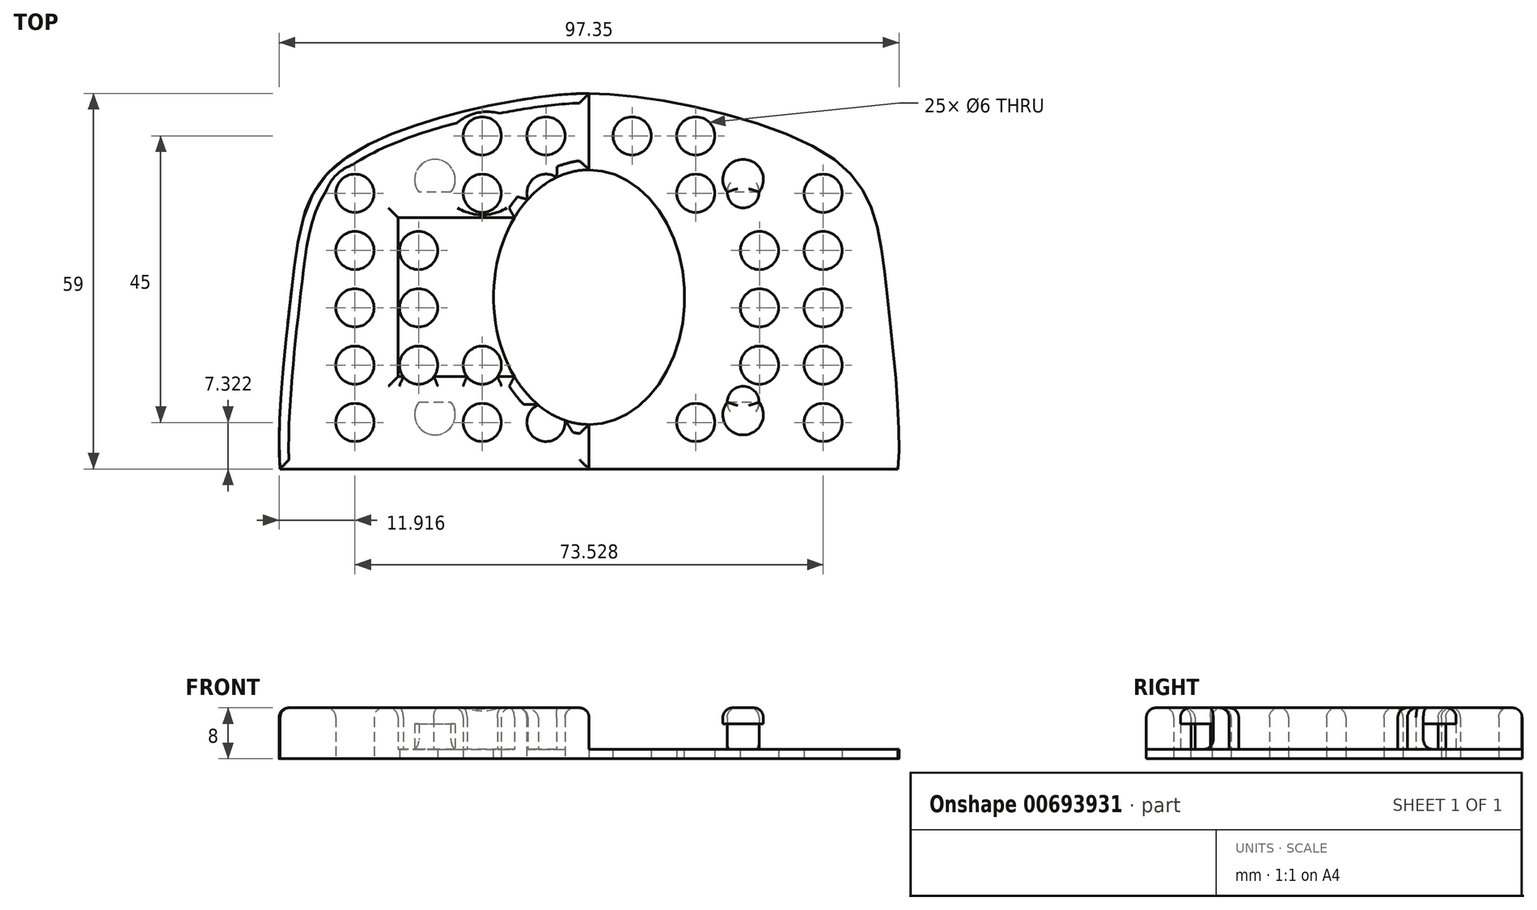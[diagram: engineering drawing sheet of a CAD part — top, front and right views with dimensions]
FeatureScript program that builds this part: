
annotation { "Feature Type Name" : "Feature", "Feature Type Description" : "" }
export const myFeature = defineFeature(function(context is Context, id is Id, definition is map)
    precondition{}
    {
        {
            var Q0;
            Q0=qCreatedBy(makeId("Top.planeOp"),FACE);
            var sketch = newSketch(context, id + "F0", { "sketchPlane" : qUnion([Q0])});
            skLineSegment(sketch, "E0", {"start": v(-48.5, 0) * mm, "end": v(48.5, 0) * mm});
            skLineSegment(sketch, "E1", {"start": v(0, 0) * mm, "end": v(0, 59) * mm});
            skFitSpline(sketch, "E2", {"points": [v(-48.5, 0) * mm, v(-46.5, 30) * mm, v(-38, 49) * mm, v(0, 59) * mm], "startDerivative": vector(-6.1, 58.21) * mm, "endDerivative": vector(65.23, -0.68) * mm});
            skFitSpline(sketch, "E3.MirrorCS", {"points": [v(48.5, 0) * mm, v(46.5, 30) * mm, v(38, 49) * mm, v(0, 59) * mm], "startDerivative": vector(6.1, 58.21) * mm, "endDerivative": vector(-65.23, -0.68) * mm});
            skEllipse(sketch, "E4", {"center": v(0, 27) * mm, "majorRadius": 20 * mm, "minorRadius": 15 * mm, "majorAxis": v(0, 1)});
            skLineSegment(sketch, "E5.bottom", {"start": v(30, 39.5) * mm, "end": v(-30, 39.5) * mm});
            skLineSegment(sketch, "E5.top", {"start": v(30, 14.5) * mm, "end": v(-30, 14.5) * mm});
            skLineSegment(sketch, "E5.left", {"start": v(30, 39.5) * mm, "end": v(30, 14.5) * mm});
            skLineSegment(sketch, "E5.right", {"start": v(-30, 39.5) * mm, "end": v(-30, 14.5) * mm});
            skArc(sketch, "E6", {"start": v(-26.7, 43.5) * mm, "mid": v(-24.2, 41) * mm, "end": v(-21.7, 43.5) * mm});
            skLineSegment(sketch, "E7", {"start": v(-26.7, 43.5) * mm, "end": v(-21.7, 43.5) * mm});
            skLineSegment(sketch, "E8", {"start": v(0, 27) * mm, "end": v(-30, 27) * mm});
            skArc(sketch, "E9.MirrorC", {"start": v(-26.7, 10.5) * mm, "mid": v(-24.2, 13) * mm, "end": v(-21.7, 10.5) * mm});
            skLineSegment(sketch, "E10.MirrorCS", {"start": v(-26.7, 10.5) * mm, "end": v(-21.7, 10.5) * mm});
            skLineSegment(sketch, "E11.MirrorCS", {"start": v(0, 54) * mm, "end": v(0, -5) * mm});
            skArc(sketch, "E12.MirrorC", {"start": v(26.7, 43.5) * mm, "mid": v(24.2, 41) * mm, "end": v(21.7, 43.5) * mm});
            skLineSegment(sketch, "E13.MirrorCS", {"start": v(26.7, 43.5) * mm, "end": v(21.7, 43.5) * mm});
            skArc(sketch, "E14.MirrorC", {"start": v(26.7, 10.5) * mm, "mid": v(24.2, 13) * mm, "end": v(21.7, 10.5) * mm});
            skLineSegment(sketch, "E15.MirrorCS", {"start": v(26.7, 10.5) * mm, "end": v(21.7, 10.5) * mm});
            skCircle(sketch, "E16", {"center": v(-6.76, 52.32) * mm, "radius": 3 * mm});
            skCircle(sketch, "E17.0.1.0", {"center": v(-6.76, 43.32) * mm, "radius": 3 * mm});
            skCircle(sketch, "E17.0.2.0", {"center": v(-6.76, 34.32) * mm, "radius": 3 * mm});
            skCircle(sketch, "E17.0.3.0", {"center": v(-6.76, 25.32) * mm, "radius": 3 * mm});
            skCircle(sketch, "E17.0.4.0", {"center": v(-6.76, 16.32) * mm, "radius": 3 * mm});
            skCircle(sketch, "E17.0.5.0", {"center": v(-6.76, 7.32) * mm, "radius": 3 * mm});
            skCircle(sketch, "E17.1.0.0", {"center": v(-16.76, 52.32) * mm, "radius": 3 * mm});
            skCircle(sketch, "E17.1.1.0", {"center": v(-16.76, 43.32) * mm, "radius": 3 * mm});
            skCircle(sketch, "E17.1.2.0", {"center": v(-16.76, 34.32) * mm, "radius": 3 * mm});
            skCircle(sketch, "E17.1.3.0", {"center": v(-16.76, 25.32) * mm, "radius": 3 * mm});
            skCircle(sketch, "E17.1.4.0", {"center": v(-16.76, 16.32) * mm, "radius": 3 * mm});
            skCircle(sketch, "E17.1.5.0", {"center": v(-16.76, 7.32) * mm, "radius": 3 * mm});
            skCircle(sketch, "E17.2.2.0", {"center": v(-26.76, 34.32) * mm, "radius": 3 * mm});
            skCircle(sketch, "E17.2.3.0", {"center": v(-26.76, 25.32) * mm, "radius": 3 * mm});
            skCircle(sketch, "E17.2.4.0", {"center": v(-26.76, 16.32) * mm, "radius": 3 * mm});
            skCircle(sketch, "E17.3.1.0", {"center": v(-36.76, 43.32) * mm, "radius": 3 * mm});
            skCircle(sketch, "E17.3.2.0", {"center": v(-36.76, 34.32) * mm, "radius": 3 * mm});
            skCircle(sketch, "E17.3.3.0", {"center": v(-36.76, 25.32) * mm, "radius": 3 * mm});
            skCircle(sketch, "E17.3.4.0", {"center": v(-36.76, 16.32) * mm, "radius": 3 * mm});
            skCircle(sketch, "E17.3.5.0", {"center": v(-36.76, 7.32) * mm, "radius": 3 * mm});
            skLineSegment(sketch, "E17.direction1", {"start": v(-6.76, 52.32) * mm, "end": v(-16.76, 52.32) * mm, "construction": true});
            skLineSegment(sketch, "E17.direction2", {"start": v(-6.76, 52.32) * mm, "end": v(-6.76, 43.32) * mm, "construction": true});
            skCircle(sketch, "E18.MirrorC", {"center": v(6.76, 52.32) * mm, "radius": 3 * mm});
            skCircle(sketch, "E19.MirrorC", {"center": v(16.76, 52.32) * mm, "radius": 3 * mm});
            skCircle(sketch, "E20.MirrorC", {"center": v(16.76, 43.32) * mm, "radius": 3 * mm});
            skCircle(sketch, "E21.MirrorC", {"center": v(36.76, 43.32) * mm, "radius": 3 * mm});
            skCircle(sketch, "E22.MirrorC", {"center": v(6.76, 43.32) * mm, "radius": 3 * mm});
            skCircle(sketch, "E23.MirrorC", {"center": v(6.76, 34.32) * mm, "radius": 3 * mm});
            skCircle(sketch, "E24.MirrorC", {"center": v(16.76, 34.32) * mm, "radius": 3 * mm});
            skCircle(sketch, "E25.MirrorC", {"center": v(26.76, 34.32) * mm, "radius": 3 * mm});
            skCircle(sketch, "E26.MirrorC", {"center": v(36.76, 34.32) * mm, "radius": 3 * mm});
            skCircle(sketch, "E27.MirrorC", {"center": v(36.76, 25.32) * mm, "radius": 3 * mm});
            skCircle(sketch, "E28.MirrorC", {"center": v(26.76, 25.32) * mm, "radius": 3 * mm});
            skCircle(sketch, "E29.MirrorC", {"center": v(16.76, 25.32) * mm, "radius": 3 * mm});
            skCircle(sketch, "E30.MirrorC", {"center": v(6.76, 25.32) * mm, "radius": 3 * mm});
            skCircle(sketch, "E31.MirrorC", {"center": v(6.76, 16.32) * mm, "radius": 3 * mm});
            skCircle(sketch, "E32.MirrorC", {"center": v(16.76, 16.32) * mm, "radius": 3 * mm});
            skCircle(sketch, "E33.MirrorC", {"center": v(26.76, 16.32) * mm, "radius": 3 * mm});
            skCircle(sketch, "E34.MirrorC", {"center": v(36.76, 16.32) * mm, "radius": 3 * mm});
            skCircle(sketch, "E35.MirrorC", {"center": v(36.76, 7.32) * mm, "radius": 3 * mm});
            skCircle(sketch, "E36.MirrorC", {"center": v(16.76, 7.32) * mm, "radius": 3 * mm});
            skCircle(sketch, "E37.MirrorC", {"center": v(6.76, 7.32) * mm, "radius": 3 * mm});
            skArc(sketch, "E38", {"start": v(-21.7, 43.5) * mm, "mid": v(-24.2, 48.64) * mm, "end": v(-26.7, 43.5) * mm});
            skArc(sketch, "E39.MirrorCS", {"start": v(21.7, 43.5) * mm, "mid": v(24.2, 48.64) * mm, "end": v(26.7, 43.5) * mm});
            skArc(sketch, "E40.MirrorCS", {"start": v(-21.7, 10.5) * mm, "mid": v(-24.2, 5.36) * mm, "end": v(-26.7, 10.5) * mm});
            skArc(sketch, "E41.MirrorCS", {"start": v(21.7, 10.5) * mm, "mid": v(24.2, 5.36) * mm, "end": v(26.7, 10.5) * mm});
            skSolve(sketch);
        }
        {
            var Q0;
            Q0 = qSketchRegion(id + "F0", true);
            var Q1;
            {var subQ0=sQuery(id+"F0.wireOp",EDGE,"E5.bottom");var subQ1=sQuery(id+"F0.wireOp",EDGE,"E4");var subQ2=makeQuery(id+"F0.imprint","INTERSECT",VERTEX,{"disambiguationData":[OD(0.0)],"derivedFrom":[subQ1,subQ0]});Q1=makeQuery(id+"F0.imprint","IMPRINT",FACE,{"disambiguationData":[TD([[makeQuery(id+"F0.imprint","IMPRINT",EDGE,{"disambiguationData":[TD([[subQ2,-1.0]])],"derivedFrom":subQ1}),-1.0]])]});}
            var Q2;
            {var subQ5=sQuery(id+"F0.wireOp",EDGE,"E5.left");Q2=makeQuery(id+"F0.imprint","IMPRINT",FACE,{"disambiguationData":[TD([[makeQuery(id+"F0.imprint","IMPRINT",EDGE,{"derivedFrom":subQ5}),-1.0]])]});}
            var Q3;
            {var subQ8=sQuery(id+"F0.wireOp",EDGE,"E17.1.3.0");var subQ9=sQuery(id+"F0.wireOp",EDGE,"E4");var subQ10=makeQuery(id+"F0.imprint","INTERSECT",VERTEX,{"disambiguationData":[OD(1.0)],"derivedFrom":[subQ9,subQ8]});Q3=makeQuery(id+"F0.imprint","IMPRINT",FACE,{"disambiguationData":[TD([[makeQuery(id+"F0.imprint","IMPRINT",EDGE,{"disambiguationData":[TD([[subQ10,-1.0]])],"derivedFrom":subQ9}),-1.0]])]});}
            var Q4;
            {var subQ0=sQuery(id+"F0.wireOp",EDGE,"E8");var subQ1=sQuery(id+"F0.wireOp",EDGE,"E4");var subQ2=makeQuery(id+"F0.imprint","INTERSECT",VERTEX,{"derivedFrom":[subQ1,subQ0]});Q4=makeQuery(id+"F0.imprint","IMPRINT",FACE,{"disambiguationData":[TD([[makeQuery(id+"F0.imprint","IMPRINT",EDGE,{"disambiguationData":[TD([[subQ2,-1.0]])],"derivedFrom":subQ1}),-1.0]])]});}
            var Q5;
            {var subQ0=sQuery(id+"F0.wireOp",EDGE,"E17.1.3.0");var subQ1=sQuery(id+"F0.wireOp",EDGE,"E4");var subQ2=makeQuery(id+"F0.imprint","INTERSECT",VERTEX,{"disambiguationData":[OD(0.0)],"derivedFrom":[subQ1,subQ0]});Q5=makeQuery(id+"F0.imprint","IMPRINT",FACE,{"disambiguationData":[TD([[makeQuery(id+"F0.imprint","IMPRINT",EDGE,{"disambiguationData":[TD([[subQ2,-1.0]])],"derivedFrom":subQ1}),-1.0]])]});}
            var Q6;
            {var subQ0=sQuery(id+"F0.wireOp",EDGE,"E17.0.1.0");var subQ1=sQuery(id+"F0.wireOp",EDGE,"E4");var subQ2=makeQuery(id+"F0.imprint","INTERSECT",VERTEX,{"disambiguationData":[OD(0.0)],"derivedFrom":[subQ1,subQ0]});Q6=makeQuery(id+"F0.imprint","IMPRINT",FACE,{"disambiguationData":[TD([[makeQuery(id+"F0.imprint","IMPRINT",EDGE,{"disambiguationData":[TD([[subQ2,-1.0]])],"derivedFrom":subQ1}),-1.0]])]});}
            var Q7;
            {var subQ0=sQuery(id+"F0.wireOp",EDGE,"E22.MirrorC");var subQ1=sQuery(id+"F0.wireOp",EDGE,"E4");var subQ2=makeQuery(id+"F0.imprint","INTERSECT",VERTEX,{"disambiguationData":[OD(0.0)],"derivedFrom":[subQ1,subQ0]});Q7=makeQuery(id+"F0.imprint","IMPRINT",FACE,{"disambiguationData":[TD([[makeQuery(id+"F0.imprint","IMPRINT",EDGE,{"disambiguationData":[TD([[subQ2,-1.0]])],"derivedFrom":subQ1}),-1.0]])]});}
            var Q8;
            {var subQ0=sQuery(id+"F0.wireOp",EDGE,"E17.0.5.0");var subQ1=sQuery(id+"F0.wireOp",EDGE,"E4");var subQ2=makeQuery(id+"F0.imprint","INTERSECT",VERTEX,{"disambiguationData":[OD(0.0)],"derivedFrom":[subQ1,subQ0]});Q8=makeQuery(id+"F0.imprint","IMPRINT",FACE,{"disambiguationData":[TD([[makeQuery(id+"F0.imprint","IMPRINT",EDGE,{"disambiguationData":[TD([[subQ2,-1.0]])],"derivedFrom":subQ1}),-1.0]])]});}
            var Q9;
            {var subQ0=sQuery(id+"F0.wireOp",EDGE,"E37.MirrorC");var subQ1=sQuery(id+"F0.wireOp",EDGE,"E4");var subQ2=makeQuery(id+"F0.imprint","INTERSECT",VERTEX,{"disambiguationData":[OD(0.0)],"derivedFrom":[subQ1,subQ0]});Q9=makeQuery(id+"F0.imprint","IMPRINT",FACE,{"disambiguationData":[TD([[makeQuery(id+"F0.imprint","IMPRINT",EDGE,{"disambiguationData":[TD([[subQ2,-1.0]])],"derivedFrom":subQ1}),-1.0]])]});}
            var Q10;
            {var subQ0=sQuery(id+"F0.wireOp",EDGE,"E29.MirrorC");var subQ1=sQuery(id+"F0.wireOp",EDGE,"E4");var subQ2=makeQuery(id+"F0.imprint","INTERSECT",VERTEX,{"disambiguationData":[OD(0.0)],"derivedFrom":[subQ1,subQ0]});Q10=makeQuery(id+"F0.imprint","IMPRINT",FACE,{"disambiguationData":[TD([[makeQuery(id+"F0.imprint","IMPRINT",EDGE,{"disambiguationData":[TD([[subQ2,-1.0]])],"derivedFrom":subQ1}),-1.0]])]});}
            var Q11;
            {var subQ0=sQuery(id+"F0.wireOp",EDGE,"E17.1.2.0");var subQ1=sQuery(id+"F0.wireOp",EDGE,"E4");var subQ2=makeQuery(id+"F0.imprint","INTERSECT",VERTEX,{"disambiguationData":[OD(0.0)],"derivedFrom":[subQ1,subQ0]});Q11=makeQuery(id+"F0.imprint","IMPRINT",FACE,{"disambiguationData":[TD([[makeQuery(id+"F0.imprint","IMPRINT",EDGE,{"disambiguationData":[TD([[subQ2,-1.0]])],"derivedFrom":subQ1}),-1.0]])]});}
            var Q12;
            {var subQ0=sQuery(id+"F0.wireOp",EDGE,"E24.MirrorC");var subQ1=sQuery(id+"F0.wireOp",EDGE,"E4");var subQ2=makeQuery(id+"F0.imprint","INTERSECT",VERTEX,{"disambiguationData":[OD(0.0)],"derivedFrom":[subQ1,subQ0]});Q12=makeQuery(id+"F0.imprint","IMPRINT",FACE,{"disambiguationData":[TD([[makeQuery(id+"F0.imprint","IMPRINT",EDGE,{"disambiguationData":[TD([[subQ2,-1.0]])],"derivedFrom":subQ1}),-1.0]])]});}
            var Q13;
            {var subQ0=sQuery(id+"F0.wireOp",EDGE,"E17.1.4.0");var subQ1=sQuery(id+"F0.wireOp",EDGE,"E5.top");var subQ2=makeQuery(id+"F0.imprint","INTERSECT",VERTEX,{"disambiguationData":[OD(0.0)],"derivedFrom":[subQ1,subQ0]});Q13=makeQuery(id+"F0.imprint","IMPRINT",FACE,{"disambiguationData":[TD([[makeQuery(id+"F0.imprint","IMPRINT",EDGE,{"disambiguationData":[TD([[subQ2,-1.0]])],"derivedFrom":subQ1}),-1.0]])]});}
            var Q14;
            {var subQ0=sQuery(id+"F0.wireOp",EDGE,"E32.MirrorC");var subQ1=sQuery(id+"F0.wireOp",EDGE,"E5.top");var subQ2=makeQuery(id+"F0.imprint","INTERSECT",VERTEX,{"disambiguationData":[OD(0.0)],"derivedFrom":[subQ1,subQ0]});Q14=makeQuery(id+"F0.imprint","IMPRINT",FACE,{"disambiguationData":[TD([[makeQuery(id+"F0.imprint","IMPRINT",EDGE,{"disambiguationData":[TD([[subQ2,-1.0]])],"derivedFrom":subQ1}),-1.0]])]});}
            var Q15;
            {var subQ0=sQuery(id+"F0.wireOp",EDGE,"E17.1.4.0");var subQ1=sQuery(id+"F0.wireOp",EDGE,"E5.top");var subQ2=makeQuery(id+"F0.imprint","INTERSECT",VERTEX,{"disambiguationData":[OD(0.0)],"derivedFrom":[subQ1,subQ0]});Q15=makeQuery(id+"F0.imprint","IMPRINT",FACE,{"disambiguationData":[TD([[makeQuery(id+"F0.imprint","IMPRINT",EDGE,{"disambiguationData":[TD([[subQ2,-1.0]])],"derivedFrom":subQ1}),1.0]])]});}
            var Q16;
            {var subQ0=sQuery(id+"F0.wireOp",EDGE,"E32.MirrorC");var subQ1=sQuery(id+"F0.wireOp",EDGE,"E5.top");var subQ2=makeQuery(id+"F0.imprint","INTERSECT",VERTEX,{"disambiguationData":[OD(0.0)],"derivedFrom":[subQ1,subQ0]});Q16=makeQuery(id+"F0.imprint","IMPRINT",FACE,{"disambiguationData":[TD([[makeQuery(id+"F0.imprint","IMPRINT",EDGE,{"disambiguationData":[TD([[subQ2,-1.0]])],"derivedFrom":subQ1}),1.0]])]});}
            var Q17;
            Q17=makeQuery(id+"F0.imprint","IMPRINT",FACE,{"disambiguationData":[TD([[makeQuery(id+"F0.imprint","IMPRINT",EDGE,{"derivedFrom":sQuery(id+"F0.wireOp",EDGE,"E6")}),1.0]])]});
            var Q18;
            Q18=makeQuery(id+"F0.imprint","IMPRINT",FACE,{"disambiguationData":[TD([[makeQuery(id+"F0.imprint","IMPRINT",EDGE,{"derivedFrom":sQuery(id+"F0.wireOp",EDGE,"E7")}),1.0]])]});
            var Q19;
            Q19=makeQuery(id+"F0.imprint","IMPRINT",FACE,{"disambiguationData":[TD([[makeQuery(id+"F0.imprint","IMPRINT",EDGE,{"derivedFrom":sQuery(id+"F0.wireOp",EDGE,"E13.MirrorCS")}),-1.0]])]});
            var Q20;
            Q20=makeQuery(id+"F0.imprint","IMPRINT",FACE,{"disambiguationData":[TD([[makeQuery(id+"F0.imprint","IMPRINT",EDGE,{"derivedFrom":sQuery(id+"F0.wireOp",EDGE,"E12.MirrorC")}),-1.0]])]});
            var Q21;
            {var subQ1=sQuery(id+"F0.wireOp",EDGE,"E15.MirrorCS");Q21=makeQuery(id+"F0.imprint","IMPRINT",FACE,{"disambiguationData":[TD([[makeQuery(id+"F0.imprint","IMPRINT",EDGE,{"derivedFrom":subQ1}),-1.0]])]});}
            var Q22;
            Q22=makeQuery(id+"F0.imprint","IMPRINT",FACE,{"disambiguationData":[TD([[makeQuery(id+"F0.imprint","IMPRINT",EDGE,{"derivedFrom":sQuery(id+"F0.wireOp",EDGE,"E15.MirrorCS")}),1.0]])]});
            var Q23;
            {var subQ0=sQuery(id+"F0.wireOp",EDGE,"E10.MirrorCS");Q23=makeQuery(id+"F0.imprint","IMPRINT",FACE,{"disambiguationData":[TD([[makeQuery(id+"F0.imprint","IMPRINT",EDGE,{"derivedFrom":subQ0}),1.0]])]});}
            var Q24;
            Q24=makeQuery(id+"F0.imprint","IMPRINT",FACE,{"disambiguationData":[TD([[makeQuery(id+"F0.imprint","IMPRINT",EDGE,{"derivedFrom":sQuery(id+"F0.wireOp",EDGE,"E10.MirrorCS")}),-1.0]])]});
            extrude(context, id + "F1", {"entities" : qUnion([Q0, Q1, Q2, Q3, Q4, Q5, Q6, Q7, Q8, Q9, Q10, Q11, Q12, Q13, Q14, Q15, Q16, Q17, Q18, Q19, Q20, Q21, Q22, Q23, Q24]), "depth" : 1.5 * mm, "offsetDistance" : 25 * mm});
        }
        {
            var Q0;
            {var subQ0=sQuery(id+"F0.wireOp",EDGE,"E7");Q0=makeQuery(id+"F0.imprint","IMPRINT",FACE,{"disambiguationData":[TD([[makeQuery(id+"F0.imprint","IMPRINT",EDGE,{"derivedFrom":subQ0}),-1.0]])]});}
            var Q1;
            {var subQ0=sQuery(id+"F0.wireOp",EDGE,"E10.MirrorCS");Q1=makeQuery(id+"F0.imprint","IMPRINT",FACE,{"disambiguationData":[TD([[makeQuery(id+"F0.imprint","IMPRINT",EDGE,{"derivedFrom":subQ0}),1.0]])]});}
            var Q2;
            {var subQ0=sQuery(id+"F0.wireOp",EDGE,"E15.MirrorCS");Q2=makeQuery(id+"F0.imprint","IMPRINT",FACE,{"disambiguationData":[TD([[makeQuery(id+"F0.imprint","IMPRINT",EDGE,{"derivedFrom":subQ0}),-1.0]])]});}
            var Q3;
            {var subQ0=sQuery(id+"F0.wireOp",EDGE,"E13.MirrorCS");Q3=makeQuery(id+"F0.imprint","IMPRINT",FACE,{"disambiguationData":[TD([[makeQuery(id+"F0.imprint","IMPRINT",EDGE,{"derivedFrom":subQ0}),1.0]])]});}
            var Q4;
            {var subQ0=sQuery(id+"F0.wireOp",EDGE,"E17.2.4.0");var subQ1=sQuery(id+"F0.wireOp",EDGE,"E9.MirrorC");var subQ2=makeQuery(id+"F0.imprint","INTERSECT",VERTEX,{"disambiguationData":[OD(0.0)],"derivedFrom":[subQ1,subQ0]});Q4=makeQuery(id+"F0.imprint","IMPRINT",FACE,{"disambiguationData":[TD([[makeQuery(id+"F0.imprint","IMPRINT",EDGE,{"disambiguationData":[TD([[subQ2,-1.0]])],"derivedFrom":subQ1}),-1.0]])]});}
            var Q5;
            {var subQ0=sQuery(id+"F0.wireOp",EDGE,"E33.MirrorC");var subQ1=sQuery(id+"F0.wireOp",EDGE,"E14.MirrorC");var subQ2=makeQuery(id+"F0.imprint","INTERSECT",VERTEX,{"disambiguationData":[OD(0.0)],"derivedFrom":[subQ1,subQ0]});Q5=makeQuery(id+"F0.imprint","IMPRINT",FACE,{"disambiguationData":[TD([[makeQuery(id+"F0.imprint","IMPRINT",EDGE,{"disambiguationData":[TD([[subQ2,-1.0]])],"derivedFrom":subQ1}),1.0]])]});}
            extrude(context, id + "F2", {"entities" : qUnion([Q0, Q1, Q2, Q3, Q4, Q5]), "operationType" : NewBodyOperationType.ADD, "depth" : 8 * mm, "offsetDistance" : 25 * mm});
        }
        {
            var Q0;
            {var subQ0=sQuery(id+"F0.wireOp",EDGE,"E10.MirrorCS");Q0=makeQuery(id+"F0.imprint","IMPRINT",FACE,{"disambiguationData":[TD([[makeQuery(id+"F0.imprint","IMPRINT",EDGE,{"derivedFrom":subQ0}),-1.0]])]});}
            var Q1;
            {var subQ0=sQuery(id+"F0.wireOp",EDGE,"E15.MirrorCS");Q1=makeQuery(id+"F0.imprint","IMPRINT",FACE,{"disambiguationData":[TD([[makeQuery(id+"F0.imprint","IMPRINT",EDGE,{"derivedFrom":subQ0}),1.0]])]});}
            var Q2;
            {var subQ0=sQuery(id+"F0.wireOp",EDGE,"E7");Q2=makeQuery(id+"F0.imprint","IMPRINT",FACE,{"disambiguationData":[TD([[makeQuery(id+"F0.imprint","IMPRINT",EDGE,{"derivedFrom":subQ0}),1.0]])]});}
            var Q3;
            {var subQ0=sQuery(id+"F0.wireOp",EDGE,"E13.MirrorCS");Q3=makeQuery(id+"F0.imprint","IMPRINT",FACE,{"disambiguationData":[TD([[makeQuery(id+"F0.imprint","IMPRINT",EDGE,{"derivedFrom":subQ0}),-1.0]])]});}
            extrude(context, id + "F3", {"entities" : qUnion([Q0, Q1, Q2, Q3]), "operationType" : NewBodyOperationType.ADD, "depth" : 8 * mm, "offsetDistance" : 25 * mm, "hasSecondDirection" : true, "secondDirectionOppositeDirection" : false, "secondDirectionDepth" : 5.5 * mm});
        }
        {
            var Q0;
            {var subQ0=sQuery(id+"F0.wireOp",EDGE,"E7");Q0=makeQuery(id+"F3.boolean.opBoolean","MERGE",FACE,{"derivedFrom":[makeQuery(id+"F2.opExtrude","CAP_FACE",FACE,{"disambiguationData":[OSD([sQuery(id+"F0.wireOp",EDGE,"E6"),subQ0])],"isStart":false}),makeQuery(id+"F3.opExtrude","CAP_FACE",FACE,{"disambiguationData":[OSD([subQ0,sQuery(id+"F0.wireOp",EDGE,"E38")])],"isStart":false})]});}
            var Q1;
            {var subQ0=sQuery(id+"F0.wireOp",EDGE,"E10.MirrorCS");Q1=makeQuery(id+"F3.boolean.opBoolean","MERGE",FACE,{"derivedFrom":[makeQuery(id+"F2.opExtrude","CAP_FACE",FACE,{"disambiguationData":[OSD([subQ0,sQuery(id+"F0.wireOp",EDGE,"E9.MirrorC"),sQuery(id+"F0.wireOp",EDGE,"E17.2.4.0")])],"isStart":false}),makeQuery(id+"F3.opExtrude","CAP_FACE",FACE,{"disambiguationData":[OSD([subQ0,sQuery(id+"F0.wireOp",EDGE,"E40.MirrorCS")])],"isStart":false})]});}
            var Q2;
            {var subQ0=sQuery(id+"F0.wireOp",EDGE,"E15.MirrorCS");Q2=makeQuery(id+"F3.boolean.opBoolean","MERGE",FACE,{"derivedFrom":[makeQuery(id+"F2.opExtrude","CAP_FACE",FACE,{"disambiguationData":[OSD([sQuery(id+"F0.wireOp",EDGE,"E14.MirrorC"),subQ0,sQuery(id+"F0.wireOp",EDGE,"E33.MirrorC")])],"isStart":false}),makeQuery(id+"F3.opExtrude","CAP_FACE",FACE,{"disambiguationData":[OSD([subQ0,sQuery(id+"F0.wireOp",EDGE,"E41.MirrorCS")])],"isStart":false})]});}
            var Q3;
            {var subQ0=sQuery(id+"F0.wireOp",EDGE,"E13.MirrorCS");Q3=makeQuery(id+"F3.boolean.opBoolean","MERGE",FACE,{"derivedFrom":[makeQuery(id+"F2.opExtrude","CAP_FACE",FACE,{"disambiguationData":[OSD([sQuery(id+"F0.wireOp",EDGE,"E12.MirrorC"),subQ0])],"isStart":false}),makeQuery(id+"F3.opExtrude","CAP_FACE",FACE,{"disambiguationData":[OSD([subQ0,sQuery(id+"F0.wireOp",EDGE,"E39.MirrorCS")])],"isStart":false})]});}
            var Q4;
            Q4=makeQuery(id+"F2.boolean.opBoolean","INTERSECT",EDGE,{"derivedFrom":[makeQuery(id+"F1.opExtrude","CAP_FACE",FACE,{"disambiguationData":[OSD([sQuery(id+"F0.wireOp",EDGE,"E0"),sQuery(id+"F0.wireOp",EDGE,"E2"),sQuery(id+"F0.wireOp",EDGE,"E3.MirrorCS"),sQuery(id+"F0.wireOp",EDGE,"E4"),sQuery(id+"F0.wireOp",EDGE,"E8"),sQuery(id+"F0.wireOp",EDGE,"E16"),sQuery(id+"F0.wireOp",EDGE,"E17.1.0.0"),sQuery(id+"F0.wireOp",EDGE,"E17.1.1.0"),sQuery(id+"F0.wireOp",EDGE,"E17.1.3.0"),sQuery(id+"F0.wireOp",EDGE,"E17.1.5.0"),sQuery(id+"F0.wireOp",EDGE,"E17.2.2.0"),sQuery(id+"F0.wireOp",EDGE,"E17.2.3.0"),sQuery(id+"F0.wireOp",EDGE,"E17.2.4.0"),sQuery(id+"F0.wireOp",EDGE,"E17.3.1.0"),sQuery(id+"F0.wireOp",EDGE,"E17.3.2.0"),sQuery(id+"F0.wireOp",EDGE,"E17.3.3.0"),sQuery(id+"F0.wireOp",EDGE,"E17.3.4.0"),sQuery(id+"F0.wireOp",EDGE,"E17.3.5.0"),sQuery(id+"F0.wireOp",EDGE,"E18.MirrorC"),sQuery(id+"F0.wireOp",EDGE,"E19.MirrorC"),sQuery(id+"F0.wireOp",EDGE,"E20.MirrorC"),sQuery(id+"F0.wireOp",EDGE,"E21.MirrorC"),sQuery(id+"F0.wireOp",EDGE,"E25.MirrorC"),sQuery(id+"F0.wireOp",EDGE,"E26.MirrorC"),sQuery(id+"F0.wireOp",EDGE,"E27.MirrorC"),sQuery(id+"F0.wireOp",EDGE,"E28.MirrorC"),sQuery(id+"F0.wireOp",EDGE,"E33.MirrorC"),sQuery(id+"F0.wireOp",EDGE,"E34.MirrorC"),sQuery(id+"F0.wireOp",EDGE,"E35.MirrorC"),sQuery(id+"F0.wireOp",EDGE,"E36.MirrorC")])],"isStart":false}),makeQuery(id+"F2.opExtrude","SWEPT_FACE",FACE,{"disambiguationData":[OSD([sQuery(id+"F0.wireOp",EDGE,"E7")])]})]});
            var Q5;
            Q5=makeQuery(id+"F2.boolean.opBoolean","INTERSECT",EDGE,{"derivedFrom":[makeQuery(id+"F1.opExtrude","CAP_FACE",FACE,{"disambiguationData":[OSD([sQuery(id+"F0.wireOp",EDGE,"E0"),sQuery(id+"F0.wireOp",EDGE,"E2"),sQuery(id+"F0.wireOp",EDGE,"E3.MirrorCS"),sQuery(id+"F0.wireOp",EDGE,"E4"),sQuery(id+"F0.wireOp",EDGE,"E8"),sQuery(id+"F0.wireOp",EDGE,"E16"),sQuery(id+"F0.wireOp",EDGE,"E17.1.0.0"),sQuery(id+"F0.wireOp",EDGE,"E17.1.1.0"),sQuery(id+"F0.wireOp",EDGE,"E17.1.3.0"),sQuery(id+"F0.wireOp",EDGE,"E17.1.5.0"),sQuery(id+"F0.wireOp",EDGE,"E17.2.2.0"),sQuery(id+"F0.wireOp",EDGE,"E17.2.3.0"),sQuery(id+"F0.wireOp",EDGE,"E17.2.4.0"),sQuery(id+"F0.wireOp",EDGE,"E17.3.1.0"),sQuery(id+"F0.wireOp",EDGE,"E17.3.2.0"),sQuery(id+"F0.wireOp",EDGE,"E17.3.3.0"),sQuery(id+"F0.wireOp",EDGE,"E17.3.4.0"),sQuery(id+"F0.wireOp",EDGE,"E17.3.5.0"),sQuery(id+"F0.wireOp",EDGE,"E18.MirrorC"),sQuery(id+"F0.wireOp",EDGE,"E19.MirrorC"),sQuery(id+"F0.wireOp",EDGE,"E20.MirrorC"),sQuery(id+"F0.wireOp",EDGE,"E21.MirrorC"),sQuery(id+"F0.wireOp",EDGE,"E25.MirrorC"),sQuery(id+"F0.wireOp",EDGE,"E26.MirrorC"),sQuery(id+"F0.wireOp",EDGE,"E27.MirrorC"),sQuery(id+"F0.wireOp",EDGE,"E28.MirrorC"),sQuery(id+"F0.wireOp",EDGE,"E33.MirrorC"),sQuery(id+"F0.wireOp",EDGE,"E34.MirrorC"),sQuery(id+"F0.wireOp",EDGE,"E35.MirrorC"),sQuery(id+"F0.wireOp",EDGE,"E36.MirrorC")])],"isStart":false}),makeQuery(id+"F2.opExtrude","SWEPT_FACE",FACE,{"disambiguationData":[OSD([sQuery(id+"F0.wireOp",EDGE,"E13.MirrorCS")])]})]});
            var Q6;
            Q6=makeQuery(id+"F2.boolean.opBoolean","INTERSECT",EDGE,{"derivedFrom":[makeQuery(id+"F1.opExtrude","CAP_FACE",FACE,{"disambiguationData":[OSD([sQuery(id+"F0.wireOp",EDGE,"E0"),sQuery(id+"F0.wireOp",EDGE,"E2"),sQuery(id+"F0.wireOp",EDGE,"E3.MirrorCS"),sQuery(id+"F0.wireOp",EDGE,"E4"),sQuery(id+"F0.wireOp",EDGE,"E8"),sQuery(id+"F0.wireOp",EDGE,"E16"),sQuery(id+"F0.wireOp",EDGE,"E17.1.0.0"),sQuery(id+"F0.wireOp",EDGE,"E17.1.1.0"),sQuery(id+"F0.wireOp",EDGE,"E17.1.3.0"),sQuery(id+"F0.wireOp",EDGE,"E17.1.5.0"),sQuery(id+"F0.wireOp",EDGE,"E17.2.2.0"),sQuery(id+"F0.wireOp",EDGE,"E17.2.3.0"),sQuery(id+"F0.wireOp",EDGE,"E17.2.4.0"),sQuery(id+"F0.wireOp",EDGE,"E17.3.1.0"),sQuery(id+"F0.wireOp",EDGE,"E17.3.2.0"),sQuery(id+"F0.wireOp",EDGE,"E17.3.3.0"),sQuery(id+"F0.wireOp",EDGE,"E17.3.4.0"),sQuery(id+"F0.wireOp",EDGE,"E17.3.5.0"),sQuery(id+"F0.wireOp",EDGE,"E18.MirrorC"),sQuery(id+"F0.wireOp",EDGE,"E19.MirrorC"),sQuery(id+"F0.wireOp",EDGE,"E20.MirrorC"),sQuery(id+"F0.wireOp",EDGE,"E21.MirrorC"),sQuery(id+"F0.wireOp",EDGE,"E25.MirrorC"),sQuery(id+"F0.wireOp",EDGE,"E26.MirrorC"),sQuery(id+"F0.wireOp",EDGE,"E27.MirrorC"),sQuery(id+"F0.wireOp",EDGE,"E28.MirrorC"),sQuery(id+"F0.wireOp",EDGE,"E33.MirrorC"),sQuery(id+"F0.wireOp",EDGE,"E34.MirrorC"),sQuery(id+"F0.wireOp",EDGE,"E35.MirrorC"),sQuery(id+"F0.wireOp",EDGE,"E36.MirrorC")])],"isStart":false}),makeQuery(id+"F2.opExtrude","SWEPT_FACE",FACE,{"disambiguationData":[OSD([sQuery(id+"F0.wireOp",EDGE,"E15.MirrorCS")])]})]});
            var Q7;
            Q7=makeQuery(id+"F2.boolean.opBoolean","INTERSECT",EDGE,{"derivedFrom":[makeQuery(id+"F1.opExtrude","CAP_FACE",FACE,{"disambiguationData":[OSD([sQuery(id+"F0.wireOp",EDGE,"E0"),sQuery(id+"F0.wireOp",EDGE,"E2"),sQuery(id+"F0.wireOp",EDGE,"E3.MirrorCS"),sQuery(id+"F0.wireOp",EDGE,"E4"),sQuery(id+"F0.wireOp",EDGE,"E8"),sQuery(id+"F0.wireOp",EDGE,"E16"),sQuery(id+"F0.wireOp",EDGE,"E17.1.0.0"),sQuery(id+"F0.wireOp",EDGE,"E17.1.1.0"),sQuery(id+"F0.wireOp",EDGE,"E17.1.3.0"),sQuery(id+"F0.wireOp",EDGE,"E17.1.5.0"),sQuery(id+"F0.wireOp",EDGE,"E17.2.2.0"),sQuery(id+"F0.wireOp",EDGE,"E17.2.3.0"),sQuery(id+"F0.wireOp",EDGE,"E17.2.4.0"),sQuery(id+"F0.wireOp",EDGE,"E17.3.1.0"),sQuery(id+"F0.wireOp",EDGE,"E17.3.2.0"),sQuery(id+"F0.wireOp",EDGE,"E17.3.3.0"),sQuery(id+"F0.wireOp",EDGE,"E17.3.4.0"),sQuery(id+"F0.wireOp",EDGE,"E17.3.5.0"),sQuery(id+"F0.wireOp",EDGE,"E18.MirrorC"),sQuery(id+"F0.wireOp",EDGE,"E19.MirrorC"),sQuery(id+"F0.wireOp",EDGE,"E20.MirrorC"),sQuery(id+"F0.wireOp",EDGE,"E21.MirrorC"),sQuery(id+"F0.wireOp",EDGE,"E25.MirrorC"),sQuery(id+"F0.wireOp",EDGE,"E26.MirrorC"),sQuery(id+"F0.wireOp",EDGE,"E27.MirrorC"),sQuery(id+"F0.wireOp",EDGE,"E28.MirrorC"),sQuery(id+"F0.wireOp",EDGE,"E33.MirrorC"),sQuery(id+"F0.wireOp",EDGE,"E34.MirrorC"),sQuery(id+"F0.wireOp",EDGE,"E35.MirrorC"),sQuery(id+"F0.wireOp",EDGE,"E36.MirrorC")])],"isStart":false}),makeQuery(id+"F2.opExtrude","SWEPT_FACE",FACE,{"disambiguationData":[OSD([sQuery(id+"F0.wireOp",EDGE,"E10.MirrorCS")])]})]});
            fillet(context, id + "F4", {"entities" : qUnion([Q0, Q1, Q2, Q3, Q4, Q5, Q6, Q7]), "radius" : 1.5 * mm, "tangentPropagation" : true, "allowEdgeOverflow" : false});
        }
    });
